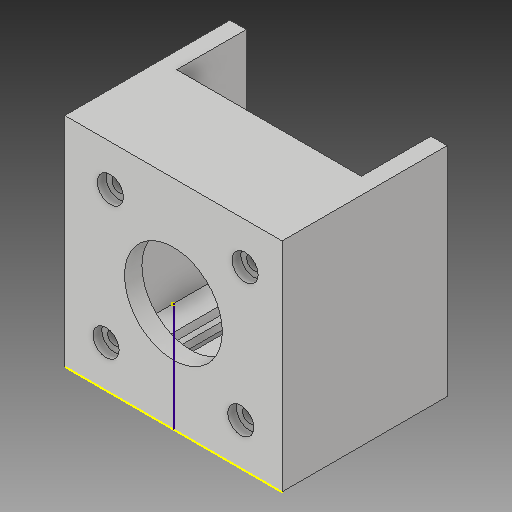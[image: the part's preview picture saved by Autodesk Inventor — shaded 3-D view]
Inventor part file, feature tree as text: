
AUTODESK INVENTOR PART (.ipt)
format: ipt  version: 2017 (Build 210142000, 142)  size: 222,720 bytes
history: native  units: in
note: dims shown in document units (in); Inventor stores cm internally (conversion verified against a paired STEP export)
features: sketch x14, extrude x8
ambient origin geometry x8: Origin, YZ Plane, XZ Plane, XY Plane, X Axis, Y Axis, Z Axis, Center Point
bodies: Solid1 (feature_tree)
feature tree (22):
  sketch  "Sketch1"  dims[d0=1.9685in d1=1.9685in]
  extrude  "Extrusion1"  Depth=1.9685in
  sketch  "Sketch3"  dims[d4=1.4961in d5=0.0in d6=1.6732in]
  extrude  "Extrusion2"  Depth=0.9843in
  extrude  "Extrusion3"  Depth=1.6732in
  sketch  "Sketch6"  dims[d12=0.7087in d13=0.0in d14=0.8858in]
  extrude  "Extrusion4"  Depth=0.1476in
  extrude  "Extrusion5"  Depth=0.1476in
  sketch  "Sketch9"  dims[d20=0.128in]
  extrude  "Extrusion6"  Depth=0.7087in
  sketch  "Sketch11"  dims[d22=1.2205in]
  extrude  "Extrusion7"  Depth=0.128in
  extrude  "Extrusion8"  Depth=0.128in
  sketch  "Sketch14"  dims[d25=1.2205in d26=0.6102in d27=0.6102in d28=0.1575in d29=0.0in d30=0.128in d31=0.128in d32=0.6693in d33=0.6693in d34=0.9843in d35=0.4921in d36=0.1575in d37=0.0in d38=0.2362in d39=0.2362in d40=0.2362in d41=0.2362in d42=0.0787in d43=0.0in d44=0.2362in d45=0.2362in d46=0.0787in d47=0.0in]
  sketch  "Sketch2"  dims[d2=0.9843in d3=0.9843in]
  sketch  "Sketch4"  dims[d7=0.6299in d8=0.1476in]
  sketch  "Sketch5"  dims[d9=1.8209in d10=0.0in d11=0.1476in]
  sketch  "Sketch7"  dims[d15=0.2362in d16=0.0in d17=0.128in]
  sketch  "Sketch8"  dims[d18=0.128in d19=0.128in]
  sketch  "Sketch10"  dims[d21=0.6102in]
  sketch  "Sketch12"  dims[d23=1.2205in]
  sketch  "Sketch13"  dims[d24=0.6102in]
